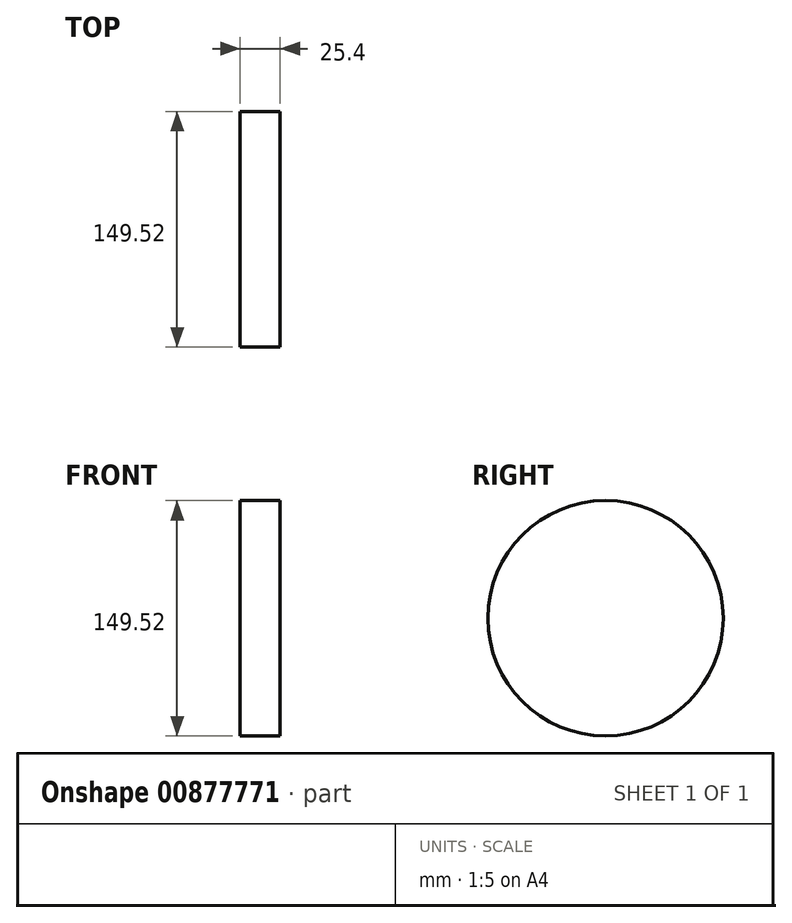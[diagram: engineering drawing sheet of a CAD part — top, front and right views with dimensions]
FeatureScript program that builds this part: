
annotation { "Feature Type Name" : "Feature", "Feature Type Description" : "" }
export const myFeature = defineFeature(function(context is Context, id is Id, definition is map)
    precondition{}
    {
        {
            var Q0;
            Q0=qCreatedBy(makeId("Right.planeOp"),FACE);
            var sketch = newSketch(context, id + "F0", { "sketchPlane" : qUnion([Q0])});
            skCircle(sketch, "E0", {"center": v(0, 0) * mm, "radius": 74.76 * mm});
            skSolve(sketch);
        }
        {
            var Q0;
            Q0 = qSketchRegion(id + "F0", true);
            var sketch = newSketch(context, id + "F1", { "sketchPlane" : qUnion([Q0])});
            skLineSegment(sketch, "E1", {"start": v(0, 0) * mm, "end": v(0, -116.81) * mm});
            skSolve(sketch);
        }
        {
            var Q0;
            Q0=makeQuery(id+"F1.imprint","IMPRINT",FACE,{"disambiguationData":[TD([[makeQuery(id+"F1.imprint","IMPRINT",EDGE,{"derivedFrom":makeQuery(id+"F0.imprint","IMPRINT",EDGE,{"derivedFrom":sQuery(id+"F0.wireOp",EDGE,"E0")})}),1.0]])]});
            extrude(context, id + "F2", {"entities" : qUnion([Q0]), "depth" : 25.4 * mm, "offsetDistance" : 25.4 * mm});
        }
    });
